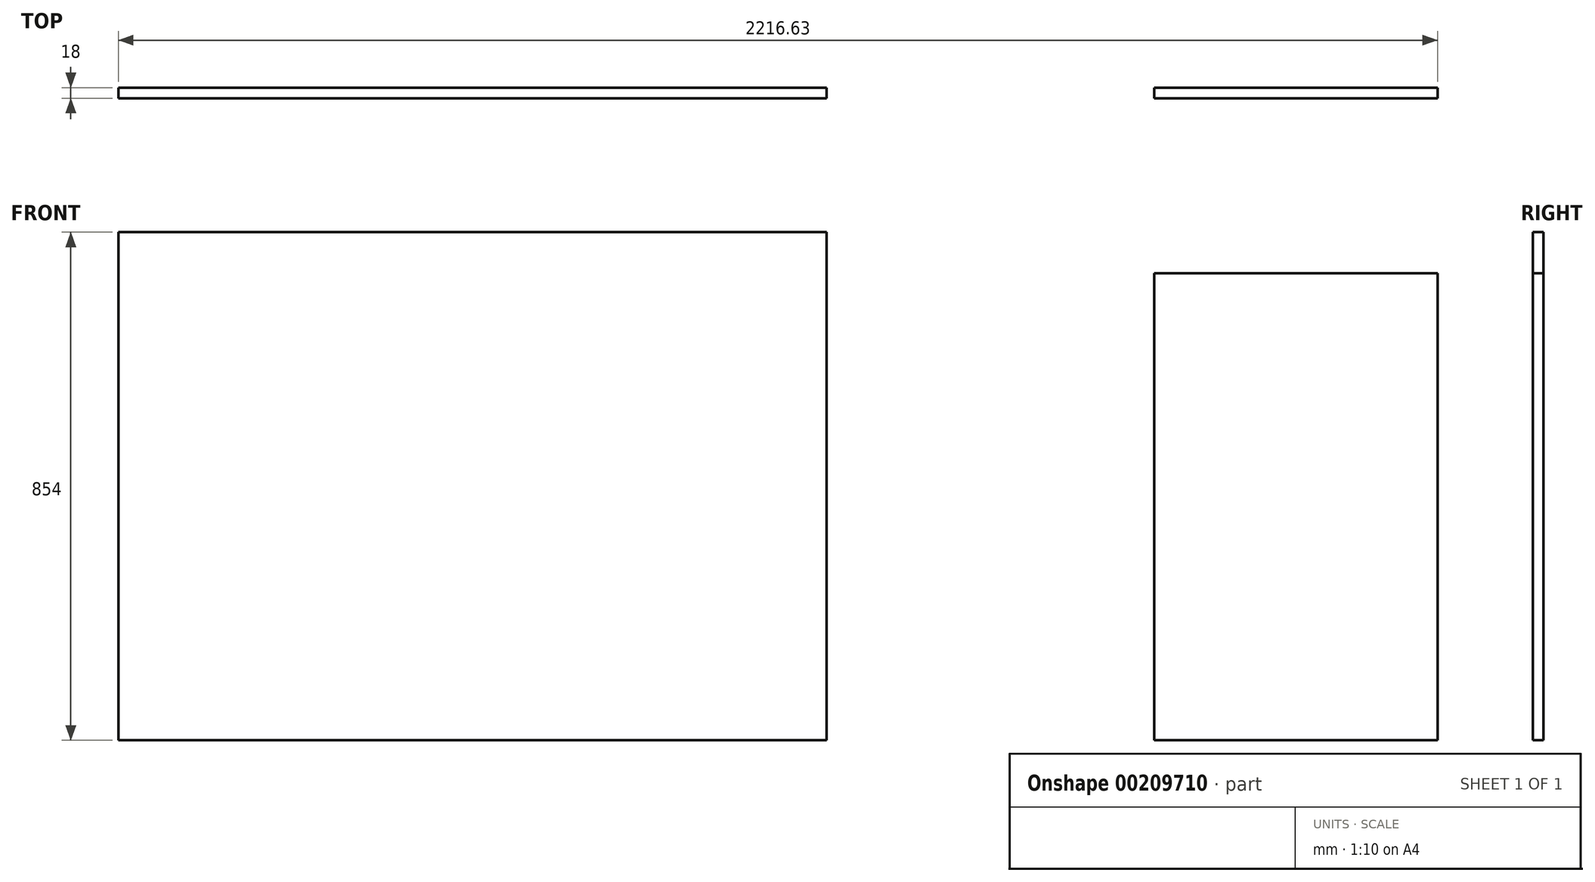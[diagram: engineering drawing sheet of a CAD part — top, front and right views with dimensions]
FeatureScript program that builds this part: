
annotation { "Feature Type Name" : "Feature", "Feature Type Description" : "" }
export const myFeature = defineFeature(function(context is Context, id is Id, definition is map)
    precondition{}
    {
        {
            var Q0;
            Q0=qCreatedBy(makeId("Front.planeOp"),FACE);
            var sketch = newSketch(context, id + "F0", { "sketchPlane" : qUnion([Q0])});
            skLineSegment(sketch, "E0.bottom", {"start": v(0, 0) * mm, "end": v(476, 0) * mm});
            skLineSegment(sketch, "E0.top", {"start": v(0, 785) * mm, "end": v(476, 785) * mm});
            skLineSegment(sketch, "E0.left", {"start": v(0, 0) * mm, "end": v(0, 785) * mm});
            skLineSegment(sketch, "E0.right", {"start": v(476, 0) * mm, "end": v(476, 785) * mm});
            skSolve(sketch);
        }
        {
            var Q0;
            Q0 = qSketchRegion(id + "F0", true);
            extrude(context, id + "F1", {"entities" : qUnion([Q0]), "depth" : 18 * mm, "offsetDistance" : 25 * mm});
        }
        {
            var Q0;
            Q0=qCreatedBy(makeId("Front.planeOp"),FACE);
            var sketch = newSketch(context, id + "F2", { "sketchPlane" : qUnion([Q0])});
            skLineSegment(sketch, "E1.bottom", {"start": v(-550.63, 0) * mm, "end": v(-1740.63, 0) * mm});
            skLineSegment(sketch, "E1.top", {"start": v(-550.63, 854) * mm, "end": v(-1740.63, 854) * mm});
            skLineSegment(sketch, "E1.left", {"start": v(-550.63, 0) * mm, "end": v(-550.63, 854) * mm});
            skLineSegment(sketch, "E1.right", {"start": v(-1740.63, 0) * mm, "end": v(-1740.63, 854) * mm});
            skSolve(sketch);
        }
        {
            var Q0;
            Q0 = qSketchRegion(id + "F2", true);
            extrude(context, id + "F3", {"entities" : qUnion([Q0]), "depth" : 18 * mm, "offsetDistance" : 25 * mm});
        }
    });
